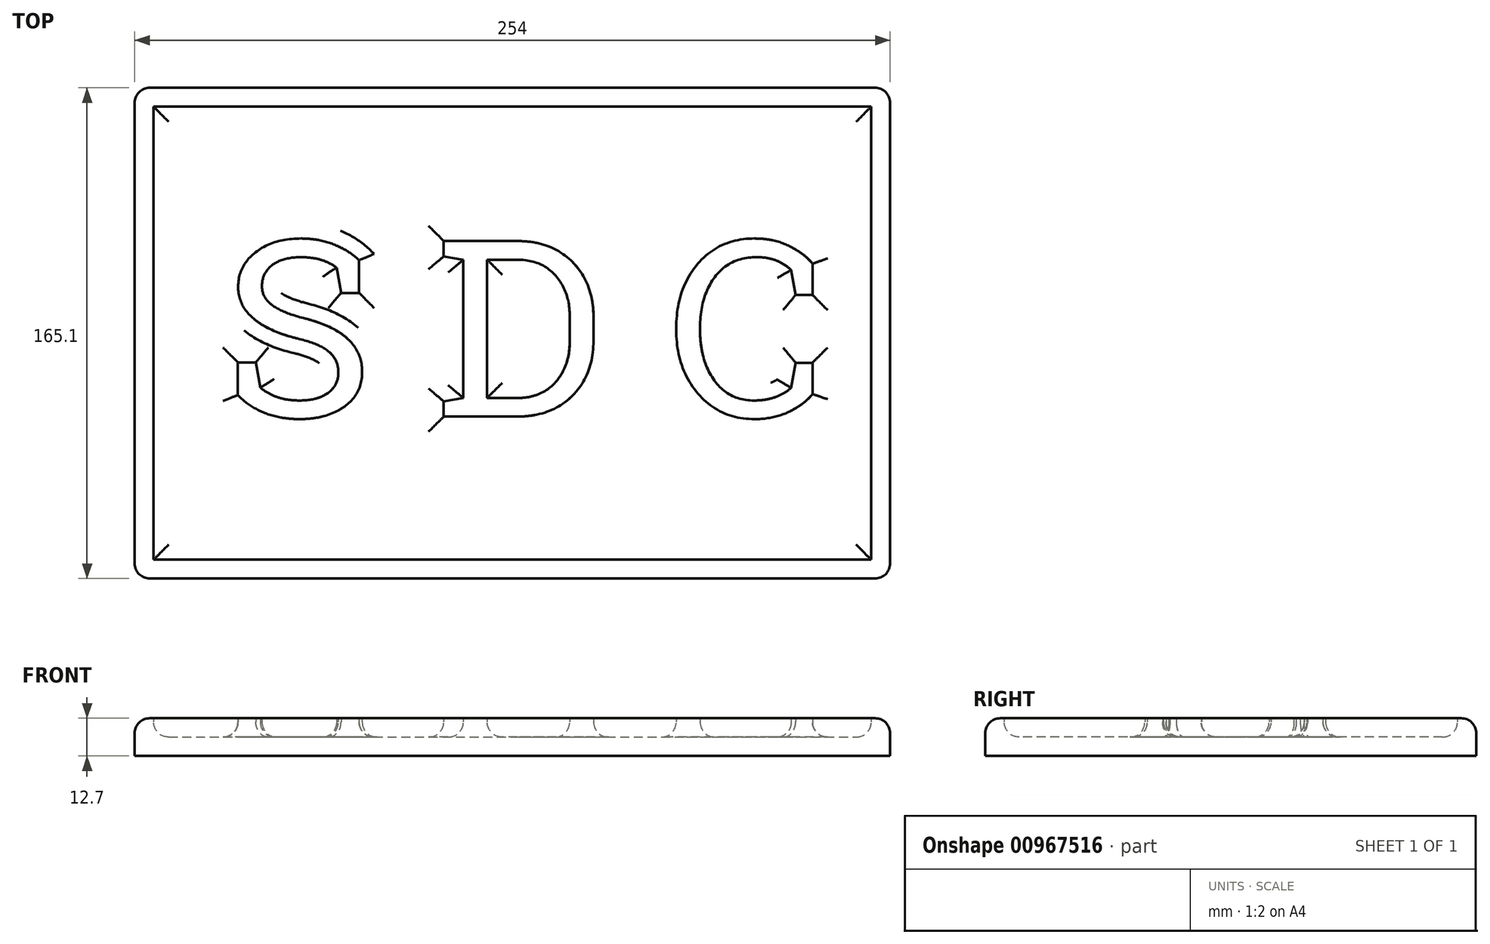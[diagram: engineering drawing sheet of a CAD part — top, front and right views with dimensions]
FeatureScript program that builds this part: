
annotation { "Feature Type Name" : "Feature", "Feature Type Description" : "" }
export const myFeature = defineFeature(function(context is Context, id is Id, definition is map)
    precondition{}
    {
        {
            var Q0;
            Q0=qCreatedBy(makeId("Top.planeOp"),FACE);
            var sketch = newSketch(context, id + "F0", { "sketchPlane" : qUnion([Q0])});
            skLineSegment(sketch, "E0.bottom", {"start": v(-131.4, 69.35) * mm, "end": v(122.6, 69.35) * mm});
            skLineSegment(sketch, "E0.top", {"start": v(-131.4, -95.75) * mm, "end": v(122.6, -95.75) * mm});
            skLineSegment(sketch, "E0.left", {"start": v(-131.4, 69.35) * mm, "end": v(-131.4, -95.75) * mm});
            skLineSegment(sketch, "E0.right", {"start": v(122.6, 69.35) * mm, "end": v(122.6, -95.75) * mm});
            skSolve(sketch);
        }
        {
            var Q0;
            Q0=makeQuery(id+"F0.imprint","IMPRINT",FACE,{"disambiguationData":[TD([[makeQuery(id+"F0.imprint","IMPRINT",EDGE,{"derivedFrom":sQuery(id+"F0.wireOp",EDGE,"E0.bottom")}),-1.0]])]});
            extrude(context, id + "F1", {"entities" : qUnion([Q0]), "depth" : -6.35 * mm, "offsetDistance" : 25.4 * mm});
        }
        {
            var Q0;
            Q0=qCreatedBy(makeId("Top.planeOp"),FACE);
            var sketch = newSketch(context, id + "F2", { "sketchPlane" : qUnion([Q0])});
            skText(sketch, "E1", { "text": "S D C", "fontName": "RobotoSlab-Regular.ttf"});
            const initialGuessF2  = {"E1": [-0.1016, -0.04125, 1, 0, 0.0598]};
            skSetInitialGuess(sketch, initialGuessF2);
            skSolve(sketch);
        }
        {
            var Q0;
            Q0 = qSketchRegion(id + "F2", true);
            extrude(context, id + "F3", {"entities" : qUnion([Q0]), "operationType" : NewBodyOperationType.ADD, "depth" : 6.35 * mm, "offsetDistance" : 25.4 * mm});
        }
        {
            var Q0;
            Q0=qCreatedBy(makeId("Top.planeOp"),FACE);
            var sketch = newSketch(context, id + "F4", { "sketchPlane" : qUnion([Q0])});
            skLineSegment(sketch, "E2.1", {"start": v(116.25, 63) * mm, "end": v(-125.05, 63) * mm});
            skLineSegment(sketch, "E2.3", {"start": v(-125.05, -89.4) * mm, "end": v(116.25, -89.4) * mm});
            skLineSegment(sketch, "E3", {"start": v(-125.05, 63) * mm, "end": v(-125.05, -89.4) * mm});
            skLineSegment(sketch, "E4.right", {"start": v(116.25, 57.78) * mm, "end": v(116.25, -84.7) * mm});
            skLineSegment(sketch, "E5", {"start": v(116.25, 63) * mm, "end": v(116.25, 57.78) * mm});
            skLineSegment(sketch, "E6", {"start": v(116.25, -84.7) * mm, "end": v(116.25, -89.4) * mm});
            skLineSegment(sketch, "E7.0", {"start": v(-131.4, 69.35) * mm, "end": v(-131.4, -95.75) * mm});
            skLineSegment(sketch, "E7.1", {"start": v(122.6, 69.35) * mm, "end": v(-131.4, 69.35) * mm});
            skLineSegment(sketch, "E7.2", {"start": v(122.6, -95.75) * mm, "end": v(122.6, 69.35) * mm});
            skLineSegment(sketch, "E7.3", {"start": v(-131.4, -95.75) * mm, "end": v(122.6, -95.75) * mm});
            skSolve(sketch);
        }
        {
            var Q0;
            Q0 = qSketchRegion(id + "F4", true);
            extrude(context, id + "F5", {"entities" : qUnion([Q0]), "operationType" : NewBodyOperationType.ADD, "depth" : 6.35 * mm, "offsetDistance" : 25.4 * mm});
        }
        {
            var Q0;
            {var subQ0=sQuery(id+"F0.wireOp",EDGE,"E0.left");var subQ1=sQuery(id+"F0.wireOp",EDGE,"E0.bottom");var subQ2=sQuery(id+"F0.wireOp",EDGE,"E0.right");var subQ3=sQuery(id+"F0.wireOp",EDGE,"E0.top");Q0=makeQuery(id+"F3.boolean.opBoolean","SPLIT",FACE,{"disambiguationData":[TD([makeQuery(id+"F1.opExtrude","SWEPT_FACE",FACE,{"disambiguationData":[OSD([subQ1])]})])],"derivedFrom":makeQuery(id+"F1.opExtrude","CAP_FACE",FACE,{"disambiguationData":[OSD([subQ1,subQ3,subQ0,subQ2])],"isStart":true})});}
            fillet(context, id + "F6", {"entities" : qUnion([Q0]), "radius" : 5.08 * mm, "tangentPropagation" : true, "allowEdgeOverflow" : false});
        }
        {
            var Q0;
            Q0=makeQuery(id+"F5.opExtrude","CAP_EDGE",EDGE,{"disambiguationData":[OSD([sQuery(id+"F4.wireOp",EDGE,"E7.1")])],"isStart":false});
            var Q1;
            Q1=makeQuery(id+"F5.opExtrude","CAP_EDGE",EDGE,{"disambiguationData":[OSD([sQuery(id+"F4.wireOp",EDGE,"E7.0")])],"isStart":false});
            var Q2;
            Q2=makeQuery(id+"F5.opExtrude","CAP_EDGE",EDGE,{"disambiguationData":[OSD([sQuery(id+"F4.wireOp",EDGE,"E7.3")])],"isStart":false});
            var Q3;
            Q3=makeQuery(id+"F5.opExtrude","CAP_EDGE",EDGE,{"disambiguationData":[OSD([sQuery(id+"F4.wireOp",EDGE,"E7.2")])],"isStart":false});
            fillet(context, id + "F7", {"entities" : qUnion([Q0, Q1, Q2, Q3]), "radius" : 5.08 * mm, "tangentPropagation" : true, "allowEdgeOverflow" : false});
        }
        {
            var Q0;
            Q0=makeQuery(id+"F5.boolean.opBoolean","MERGE",EDGE,{"derivedFrom":[makeQuery(id+"F1.opExtrude","SWEPT_EDGE",EDGE,{"disambiguationData":[OSD([sQuery(id+"F0.wireOp",EDGE,"E0.top"),sQuery(id+"F0.wireOp",EDGE,"E0.left")])]}),makeQuery(id+"F5.opExtrude","SWEPT_EDGE",EDGE,{"disambiguationData":[OSD([sQuery(id+"F4.wireOp",EDGE,"E7.0"),sQuery(id+"F4.wireOp",EDGE,"E7.3")])]})]});
            var Q1;
            Q1=makeQuery(id+"F5.boolean.opBoolean","MERGE",EDGE,{"derivedFrom":[makeQuery(id+"F1.opExtrude","SWEPT_EDGE",EDGE,{"disambiguationData":[OSD([sQuery(id+"F0.wireOp",EDGE,"E0.top"),sQuery(id+"F0.wireOp",EDGE,"E0.right")])]}),makeQuery(id+"F5.opExtrude","SWEPT_EDGE",EDGE,{"disambiguationData":[OSD([sQuery(id+"F4.wireOp",EDGE,"E7.2"),sQuery(id+"F4.wireOp",EDGE,"E7.3")])]})]});
            var Q2;
            Q2=makeQuery(id+"F5.boolean.opBoolean","MERGE",EDGE,{"derivedFrom":[makeQuery(id+"F1.opExtrude","SWEPT_EDGE",EDGE,{"disambiguationData":[OSD([sQuery(id+"F0.wireOp",EDGE,"E0.bottom"),sQuery(id+"F0.wireOp",EDGE,"E0.right")])]}),makeQuery(id+"F5.opExtrude","SWEPT_EDGE",EDGE,{"disambiguationData":[OSD([sQuery(id+"F4.wireOp",EDGE,"E7.1"),sQuery(id+"F4.wireOp",EDGE,"E7.2")])]})]});
            var Q3;
            Q3=makeQuery(id+"F5.boolean.opBoolean","MERGE",EDGE,{"derivedFrom":[makeQuery(id+"F1.opExtrude","SWEPT_EDGE",EDGE,{"disambiguationData":[OSD([sQuery(id+"F0.wireOp",EDGE,"E0.bottom"),sQuery(id+"F0.wireOp",EDGE,"E0.left")])]}),makeQuery(id+"F5.opExtrude","SWEPT_EDGE",EDGE,{"disambiguationData":[OSD([sQuery(id+"F4.wireOp",EDGE,"E7.0"),sQuery(id+"F4.wireOp",EDGE,"E7.1")])]})]});
            fillet(context, id + "F8", {"entities" : qUnion([Q0, Q1, Q2, Q3]), "radius" : 5.08 * mm, "tangentPropagation" : true, "allowEdgeOverflow" : false});
        }
        {
            var Q0;
            Q0=makeQuery(id+"F3.boolean.opBoolean","SPLIT",FACE,{"disambiguationData":[TD([makeQuery(id+"F3.opExtrude","SWEPT_FACE",FACE,{"disambiguationData":[OSD([sQuery(id+"F2.wireOp",EDGE,"E1.sketch_text.stroke-43")])]})])],"derivedFrom":makeQuery(id+"F1.opExtrude","CAP_FACE",FACE,{"disambiguationData":[OSD([sQuery(id+"F0.wireOp",EDGE,"E0.bottom"),sQuery(id+"F0.wireOp",EDGE,"E0.top"),sQuery(id+"F0.wireOp",EDGE,"E0.left"),sQuery(id+"F0.wireOp",EDGE,"E0.right")])],"isStart":true})});
            fillet(context, id + "F9", {"entities" : qUnion([Q0]), "radius" : 5.08 * mm, "tangentPropagation" : true, "allowEdgeOverflow" : false});
        }
    });
